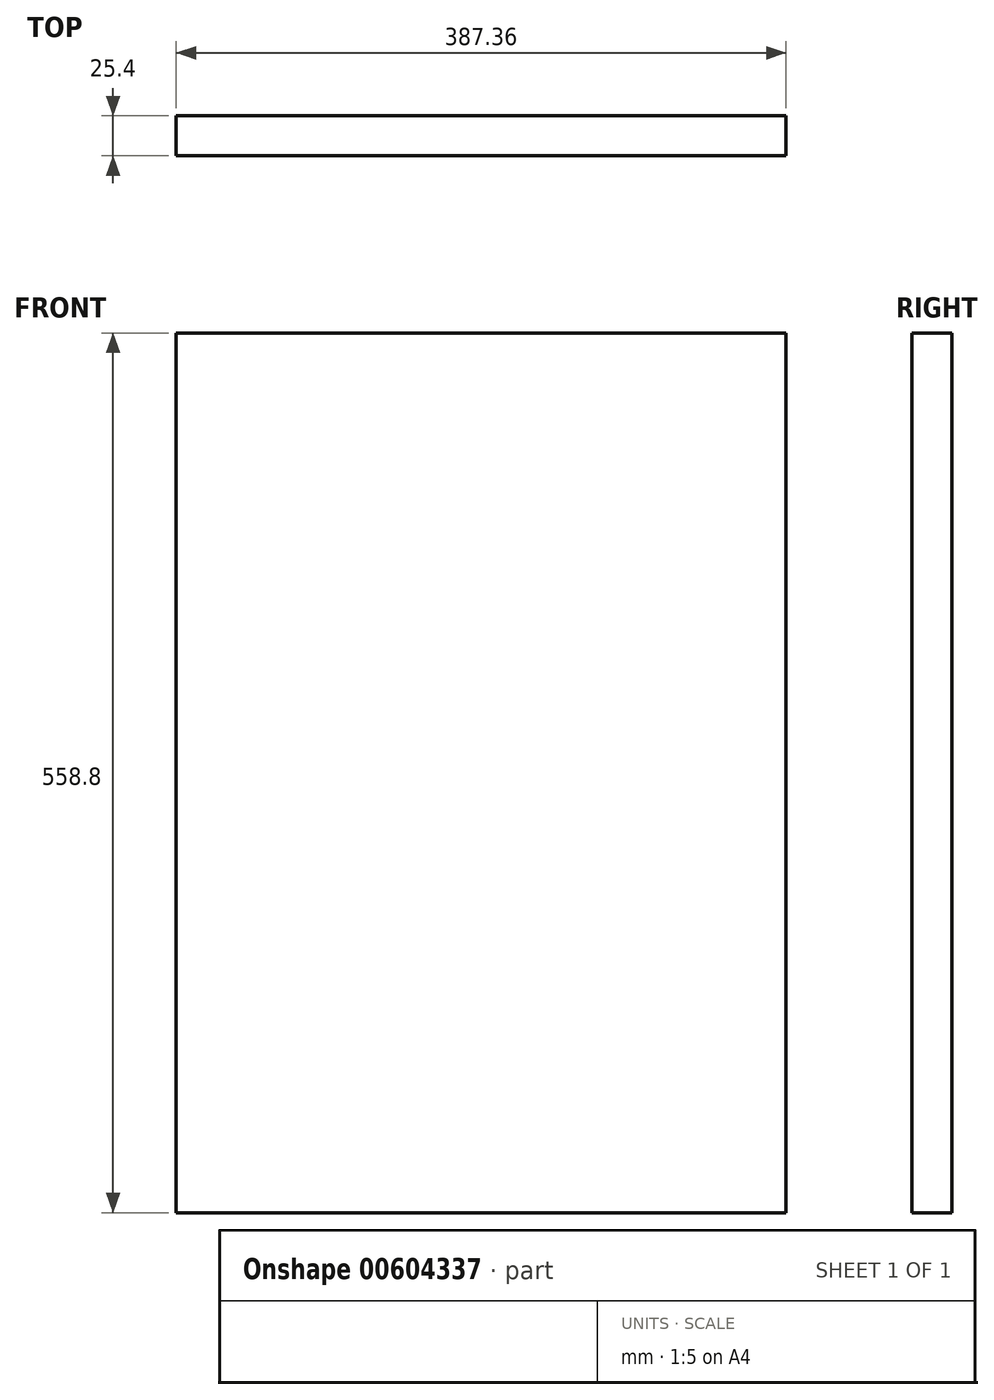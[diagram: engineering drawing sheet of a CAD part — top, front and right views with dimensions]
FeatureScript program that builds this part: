
annotation { "Feature Type Name" : "Feature", "Feature Type Description" : "" }
export const myFeature = defineFeature(function(context is Context, id is Id, definition is map)
    precondition{}
    {
        {
            var Q0;
            Q0=qCreatedBy(makeId("Front.planeOp"),FACE);
            var sketch = newSketch(context, id + "F0", { "sketchPlane" : qUnion([Q0])});
            skLineSegment(sketch, "E0.bottom", {"start": v(193.68, 279.4) * mm, "end": v(-193.68, 279.4) * mm});
            skLineSegment(sketch, "E0.top", {"start": v(193.68, -279.4) * mm, "end": v(-193.68, -279.4) * mm});
            skLineSegment(sketch, "E0.left", {"start": v(193.68, 279.4) * mm, "end": v(193.68, -279.4) * mm});
            skLineSegment(sketch, "E0.right", {"start": v(-193.67, 279.4) * mm, "end": v(-193.68, -279.4) * mm});
            skPoint(sketch, "E0.middle", {"position": v(0, 0) * mm});
            skSolve(sketch);
        }
        {
            var Q0;
            Q0 = qSketchRegion(id + "F0", true);
            extrude(context, id + "F1", {"entities" : qUnion([Q0]), "depth" : 25.4 * mm, "offsetDistance" : 25.4 * mm});
        }
    });
